# Revit family: Haworth_BuzziPouf_Square
name_source: partatom
category: Furniture
revit_build: Autodesk Revit 2018 (Build: 20170223_1515(x64)
units: mm (PartAtom-declared; Revit-internal decimal feet)

## family parameters
Always vertical = Yes
Cut with Voids When Loaded = No
OmniClass Number = 23.40.70.14.64.21
OmniClass Title = Systems Furniture
Room Calculation Point = No
Shared = No
Work Plane-Based = No

## types (2) — shared parameters
Assembly Code = E2020200
Base Finish = Haworth _ Paint _ Black BTR-9005
Manufacturer = Haworth
Model = HCBZ-PFPS
Revision Number = 1
Size = Verify Final Dim. w/ Haworth
URL = http://www.haworth.com
URL - Product = https://www.haworth.com
Warranty = http://www.haworth.com
zero-valued in all types: Actual Depth, Actual Height, Actual Width, Void, Void Length Vertical

## per-type parameters (varying)
| type | 3D | Description | Flat |
| HCBZ-PFPS-F2 | No | Haworth BuzziPouf Flat Square Pouf | Yes |
| HCBZ-PFPS-32 | Yes | Haworth BuzziPouf 3D Square Pouf | No |

## geometry (parser evidence)
native form markers: Sweep x2
no freeform markers — native parametric forms only
